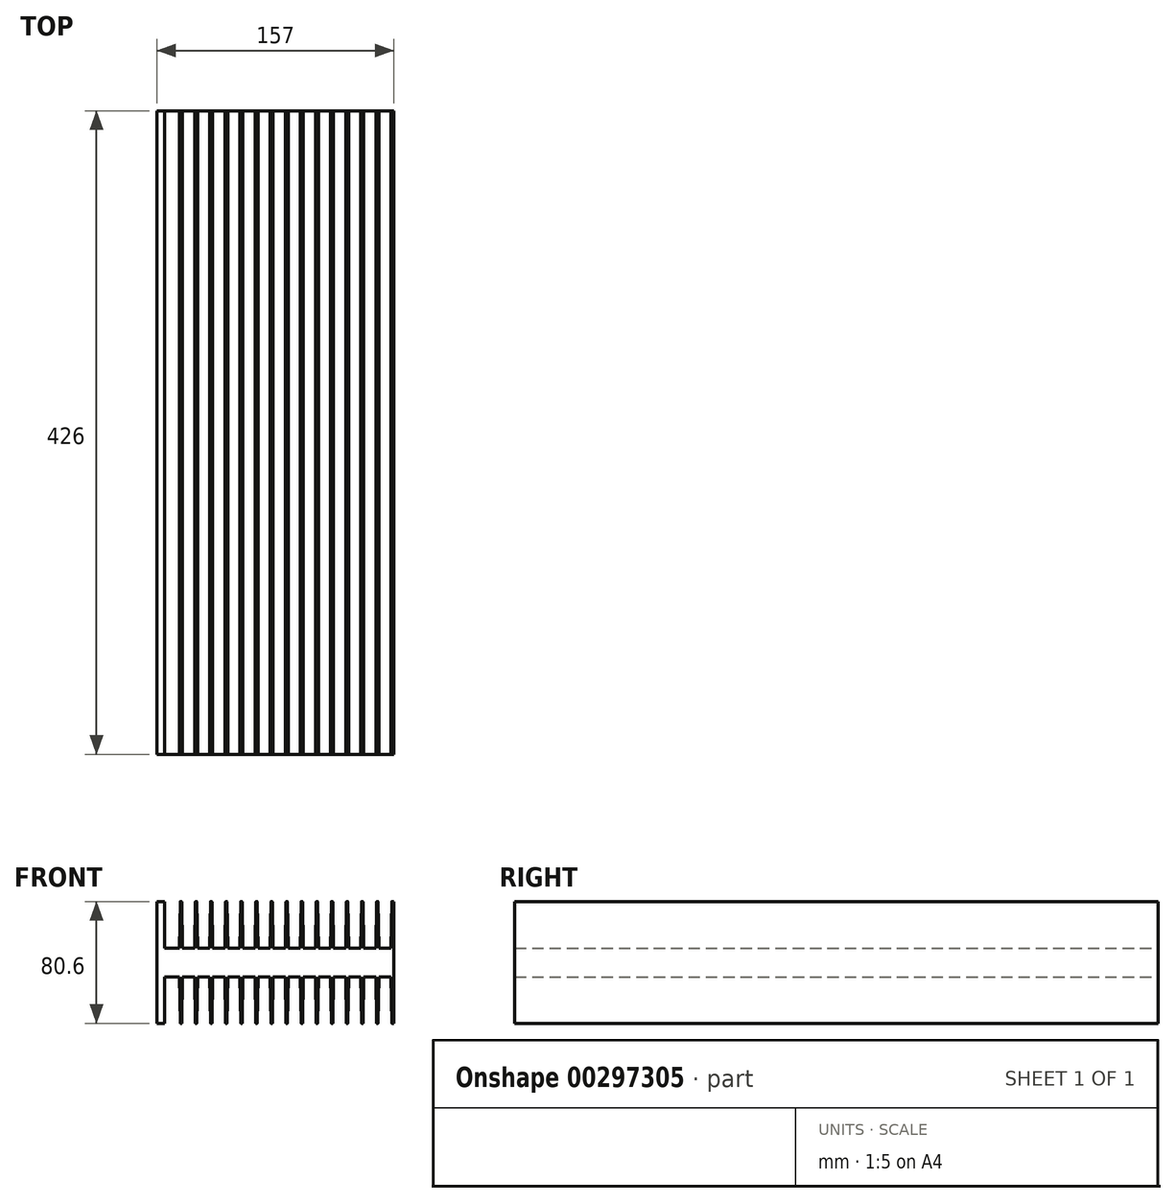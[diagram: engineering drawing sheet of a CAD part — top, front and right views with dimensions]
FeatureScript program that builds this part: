
annotation { "Feature Type Name" : "Feature", "Feature Type Description" : "" }
export const myFeature = defineFeature(function(context is Context, id is Id, definition is map)
    precondition{}
    {
        {
            var Q0;
            Q0=qCreatedBy(makeId("Front.planeOp"),FACE);
            var sketch = newSketch(context, id + "F0", { "sketchPlane" : qUnion([Q0])});
            skLineSegment(sketch, "E0", {"start": v(0, 0) * mm, "end": v(-0.5, 30.68) * mm});
            skLineSegment(sketch, "E1", {"start": v(8, 0) * mm, "end": v(8.5, 30.68) * mm});
            skLineSegment(sketch, "E2", {"start": v(-0.62, 30.8) * mm, "end": v(-1.5, 30.8) * mm});
            skLineSegment(sketch, "E3", {"start": v(-1.5, 30.8) * mm, "end": v(-2, 30.8) * mm});
            skLineSegment(sketch, "E4", {"start": v(-2, 30.8) * mm, "end": v(-2, -9.5) * mm});
            skLineSegment(sketch, "E5", {"start": v(-2, -9.5) * mm, "end": v(155, -9.5) * mm});
            skLineSegment(sketch, "E6", {"start": v(150, 30.8) * mm, "end": v(155, 30.8) * mm});
            skLineSegment(sketch, "E7", {"start": v(155, 30.8) * mm, "end": v(155, -9.5) * mm});
            skLineSegment(sketch, "E8", {"start": v(8, 0) * mm, "end": v(10, 0) * mm, "construction": true});
            skLineSegment(sketch, "E9", {"start": v(9, 0) * mm, "end": v(9, 30.8) * mm});
            skLineSegment(sketch, "E10", {"start": v(9, 30.8) * mm, "end": v(9, 0) * mm, "construction": true});
            skPoint(sketch, "E11.visualSharp", {"position": v(8.5, 30.8) * mm});
            skArc(sketch, "E11.filletArc", {"start": v(8.62, 30.8) * mm, "mid": v(8.53, 30.76) * mm, "end": v(8.5, 30.68) * mm});
            skPoint(sketch, "E12.visualSharp", {"position": v(9.5, 30.8) * mm});
            skPoint(sketch, "E13.visualSharp", {"position": v(-0.5, 30.8) * mm});
            skArc(sketch, "E13.filletArc", {"start": v(-0.5, 30.68) * mm, "mid": v(-0.53, 30.76) * mm, "end": v(-0.62, 30.8) * mm});
            skLineSegment(sketch, "E14", {"start": v(0, 0) * mm, "end": v(8, 0) * mm});
            skLineSegment(sketch, "E15", {"start": v(10, 0) * mm, "end": v(9.5, 30.68) * mm});
            skLineSegment(sketch, "E16", {"start": v(8.62, 30.8) * mm, "end": v(9.38, 30.8) * mm});
            skArc(sketch, "E17.filletArc", {"start": v(9.5, 30.68) * mm, "mid": v(9.47, 30.76) * mm, "end": v(9.38, 30.8) * mm});
            skLineSegment(sketch, "E18.1.0.0", {"start": v(10, 0) * mm, "end": v(18, 0) * mm});
            skLineSegment(sketch, "E18.1.0.1", {"start": v(18, 0) * mm, "end": v(18.5, 30.68) * mm});
            skArc(sketch, "E18.1.0.2", {"start": v(18.62, 30.8) * mm, "mid": v(18.53, 30.76) * mm, "end": v(18.5, 30.68) * mm});
            skLineSegment(sketch, "E18.1.0.3", {"start": v(18.62, 30.8) * mm, "end": v(19.38, 30.8) * mm});
            skArc(sketch, "E18.1.0.4", {"start": v(19.5, 30.68) * mm, "mid": v(19.47, 30.76) * mm, "end": v(19.38, 30.8) * mm});
            skLineSegment(sketch, "E18.1.0.5", {"start": v(20, 0) * mm, "end": v(19.5, 30.68) * mm});
            skLineSegment(sketch, "E18.2.0.0", {"start": v(20, 0) * mm, "end": v(28, 0) * mm});
            skLineSegment(sketch, "E18.2.0.1", {"start": v(28, 0) * mm, "end": v(28.5, 30.68) * mm});
            skArc(sketch, "E18.2.0.2", {"start": v(28.62, 30.8) * mm, "mid": v(28.53, 30.76) * mm, "end": v(28.5, 30.68) * mm});
            skLineSegment(sketch, "E18.2.0.3", {"start": v(28.62, 30.8) * mm, "end": v(29.38, 30.8) * mm});
            skArc(sketch, "E18.2.0.4", {"start": v(29.5, 30.68) * mm, "mid": v(29.47, 30.76) * mm, "end": v(29.38, 30.8) * mm});
            skLineSegment(sketch, "E18.2.0.5", {"start": v(30, 0) * mm, "end": v(29.5, 30.68) * mm});
            skLineSegment(sketch, "E18.3.0.0", {"start": v(30, 0) * mm, "end": v(38, 0) * mm});
            skLineSegment(sketch, "E18.3.0.1", {"start": v(38, 0) * mm, "end": v(38.5, 30.68) * mm});
            skArc(sketch, "E18.3.0.2", {"start": v(38.62, 30.8) * mm, "mid": v(38.53, 30.76) * mm, "end": v(38.5, 30.68) * mm});
            skLineSegment(sketch, "E18.3.0.3", {"start": v(38.62, 30.8) * mm, "end": v(39.38, 30.8) * mm});
            skArc(sketch, "E18.3.0.4", {"start": v(39.5, 30.68) * mm, "mid": v(39.47, 30.76) * mm, "end": v(39.38, 30.8) * mm});
            skLineSegment(sketch, "E18.3.0.5", {"start": v(40, 0) * mm, "end": v(39.5, 30.68) * mm});
            skLineSegment(sketch, "E18.4.0.0", {"start": v(40, 0) * mm, "end": v(48, 0) * mm});
            skLineSegment(sketch, "E18.4.0.1", {"start": v(48, 0) * mm, "end": v(48.5, 30.68) * mm});
            skArc(sketch, "E18.4.0.2", {"start": v(48.62, 30.8) * mm, "mid": v(48.53, 30.76) * mm, "end": v(48.5, 30.68) * mm});
            skLineSegment(sketch, "E18.4.0.3", {"start": v(48.62, 30.8) * mm, "end": v(49.38, 30.8) * mm});
            skArc(sketch, "E18.4.0.4", {"start": v(49.5, 30.68) * mm, "mid": v(49.47, 30.76) * mm, "end": v(49.38, 30.8) * mm});
            skLineSegment(sketch, "E18.4.0.5", {"start": v(50, 0) * mm, "end": v(49.5, 30.68) * mm});
            skLineSegment(sketch, "E18.5.0.0", {"start": v(50, 0) * mm, "end": v(58, 0) * mm});
            skLineSegment(sketch, "E18.5.0.1", {"start": v(58, 0) * mm, "end": v(58.5, 30.68) * mm});
            skArc(sketch, "E18.5.0.2", {"start": v(58.62, 30.8) * mm, "mid": v(58.53, 30.76) * mm, "end": v(58.5, 30.68) * mm});
            skLineSegment(sketch, "E18.5.0.3", {"start": v(58.62, 30.8) * mm, "end": v(59.38, 30.8) * mm});
            skArc(sketch, "E18.5.0.4", {"start": v(59.5, 30.68) * mm, "mid": v(59.47, 30.76) * mm, "end": v(59.38, 30.8) * mm});
            skLineSegment(sketch, "E18.5.0.5", {"start": v(60, 0) * mm, "end": v(59.5, 30.68) * mm});
            skLineSegment(sketch, "E18.6.0.0", {"start": v(60, 0) * mm, "end": v(68, 0) * mm});
            skLineSegment(sketch, "E18.6.0.1", {"start": v(68, 0) * mm, "end": v(68.5, 30.68) * mm});
            skArc(sketch, "E18.6.0.2", {"start": v(68.62, 30.8) * mm, "mid": v(68.53, 30.76) * mm, "end": v(68.5, 30.68) * mm});
            skLineSegment(sketch, "E18.6.0.3", {"start": v(68.62, 30.8) * mm, "end": v(69.38, 30.8) * mm});
            skArc(sketch, "E18.6.0.4", {"start": v(69.5, 30.68) * mm, "mid": v(69.47, 30.76) * mm, "end": v(69.38, 30.8) * mm});
            skLineSegment(sketch, "E18.6.0.5", {"start": v(70, 0) * mm, "end": v(69.5, 30.68) * mm});
            skLineSegment(sketch, "E18.7.0.0", {"start": v(70, 0) * mm, "end": v(78, 0) * mm});
            skLineSegment(sketch, "E18.7.0.1", {"start": v(78, 0) * mm, "end": v(78.5, 30.68) * mm});
            skArc(sketch, "E18.7.0.2", {"start": v(78.62, 30.8) * mm, "mid": v(78.53, 30.76) * mm, "end": v(78.5, 30.68) * mm});
            skLineSegment(sketch, "E18.7.0.3", {"start": v(78.62, 30.8) * mm, "end": v(79.38, 30.8) * mm});
            skArc(sketch, "E18.7.0.4", {"start": v(79.5, 30.68) * mm, "mid": v(79.47, 30.76) * mm, "end": v(79.38, 30.8) * mm});
            skLineSegment(sketch, "E18.7.0.5", {"start": v(80, 0) * mm, "end": v(79.5, 30.68) * mm});
            skLineSegment(sketch, "E18.8.0.0", {"start": v(80, 0) * mm, "end": v(88, 0) * mm});
            skLineSegment(sketch, "E18.8.0.1", {"start": v(88, 0) * mm, "end": v(88.5, 30.68) * mm});
            skArc(sketch, "E18.8.0.2", {"start": v(88.62, 30.8) * mm, "mid": v(88.53, 30.76) * mm, "end": v(88.5, 30.68) * mm});
            skLineSegment(sketch, "E18.8.0.3", {"start": v(88.62, 30.8) * mm, "end": v(89.38, 30.8) * mm});
            skArc(sketch, "E18.8.0.4", {"start": v(89.5, 30.68) * mm, "mid": v(89.47, 30.76) * mm, "end": v(89.38, 30.8) * mm});
            skLineSegment(sketch, "E18.8.0.5", {"start": v(90, 0) * mm, "end": v(89.5, 30.68) * mm});
            skLineSegment(sketch, "E18.9.0.0", {"start": v(90, 0) * mm, "end": v(98, 0) * mm});
            skLineSegment(sketch, "E18.9.0.1", {"start": v(98, 0) * mm, "end": v(98.5, 30.68) * mm});
            skArc(sketch, "E18.9.0.2", {"start": v(98.62, 30.8) * mm, "mid": v(98.53, 30.76) * mm, "end": v(98.5, 30.68) * mm});
            skLineSegment(sketch, "E18.9.0.3", {"start": v(98.62, 30.8) * mm, "end": v(99.38, 30.8) * mm});
            skArc(sketch, "E18.9.0.4", {"start": v(99.5, 30.68) * mm, "mid": v(99.47, 30.76) * mm, "end": v(99.38, 30.8) * mm});
            skLineSegment(sketch, "E18.9.0.5", {"start": v(100, 0) * mm, "end": v(99.5, 30.68) * mm});
            skLineSegment(sketch, "E18.10.0.0", {"start": v(100, 0) * mm, "end": v(108, 0) * mm});
            skLineSegment(sketch, "E18.10.0.1", {"start": v(108, 0) * mm, "end": v(108.5, 30.68) * mm});
            skArc(sketch, "E18.10.0.2", {"start": v(108.62, 30.8) * mm, "mid": v(108.53, 30.76) * mm, "end": v(108.5, 30.68) * mm});
            skLineSegment(sketch, "E18.10.0.3", {"start": v(108.62, 30.8) * mm, "end": v(109.38, 30.8) * mm});
            skArc(sketch, "E18.10.0.4", {"start": v(109.5, 30.68) * mm, "mid": v(109.47, 30.76) * mm, "end": v(109.38, 30.8) * mm});
            skLineSegment(sketch, "E18.10.0.5", {"start": v(110, 0) * mm, "end": v(109.5, 30.68) * mm});
            skLineSegment(sketch, "E18.11.0.0", {"start": v(110, 0) * mm, "end": v(118, 0) * mm});
            skLineSegment(sketch, "E18.11.0.1", {"start": v(118, 0) * mm, "end": v(118.5, 30.68) * mm});
            skArc(sketch, "E18.11.0.2", {"start": v(118.62, 30.8) * mm, "mid": v(118.53, 30.76) * mm, "end": v(118.5, 30.68) * mm});
            skLineSegment(sketch, "E18.11.0.3", {"start": v(118.62, 30.8) * mm, "end": v(119.38, 30.8) * mm});
            skArc(sketch, "E18.11.0.4", {"start": v(119.5, 30.68) * mm, "mid": v(119.47, 30.76) * mm, "end": v(119.38, 30.8) * mm});
            skLineSegment(sketch, "E18.11.0.5", {"start": v(120, 0) * mm, "end": v(119.5, 30.68) * mm});
            skLineSegment(sketch, "E18.12.0.0", {"start": v(120, 0) * mm, "end": v(128, 0) * mm});
            skLineSegment(sketch, "E18.12.0.1", {"start": v(128, 0) * mm, "end": v(128.5, 30.68) * mm});
            skArc(sketch, "E18.12.0.2", {"start": v(128.62, 30.8) * mm, "mid": v(128.53, 30.76) * mm, "end": v(128.5, 30.68) * mm});
            skLineSegment(sketch, "E18.12.0.3", {"start": v(128.62, 30.8) * mm, "end": v(129.38, 30.8) * mm});
            skArc(sketch, "E18.12.0.4", {"start": v(129.5, 30.68) * mm, "mid": v(129.47, 30.76) * mm, "end": v(129.38, 30.8) * mm});
            skLineSegment(sketch, "E18.12.0.5", {"start": v(130, 0) * mm, "end": v(129.5, 30.68) * mm});
            skLineSegment(sketch, "E18.13.0.0", {"start": v(130, 0) * mm, "end": v(138, 0) * mm});
            skLineSegment(sketch, "E18.13.0.1", {"start": v(138, 0) * mm, "end": v(138.5, 30.68) * mm});
            skArc(sketch, "E18.13.0.2", {"start": v(138.62, 30.8) * mm, "mid": v(138.53, 30.76) * mm, "end": v(138.5, 30.68) * mm});
            skLineSegment(sketch, "E18.13.0.3", {"start": v(138.62, 30.8) * mm, "end": v(139.38, 30.8) * mm});
            skArc(sketch, "E18.13.0.4", {"start": v(139.5, 30.68) * mm, "mid": v(139.47, 30.76) * mm, "end": v(139.38, 30.8) * mm});
            skLineSegment(sketch, "E18.13.0.5", {"start": v(140, 0) * mm, "end": v(139.5, 30.68) * mm});
            skLineSegment(sketch, "E18.direction1", {"start": v(0, 0) * mm, "end": v(10, 0) * mm, "construction": true});
            skLineSegment(sketch, "E19", {"start": v(140, 0) * mm, "end": v(150, 0) * mm});
            skLineSegment(sketch, "E20", {"start": v(150, 30.8) * mm, "end": v(150, 0) * mm});
            skSolve(sketch);
        }
        {
            var Q0;
            Q0=qSketchRegion(id+"F0",true);
            extrude(context, id + "F1", {"entities" : qUnion([Q0]), "depth" : 426 * mm});
        }
        {
            var Q0;
            Q0=makeQuery(id+"F1.opExtrude","SWEPT_BODY",BODY,{"disambiguationData":[OSD([sQuery(id+"F0.wireOp",EDGE,"E0"),sQuery(id+"F0.wireOp",EDGE,"E1"),sQuery(id+"F0.wireOp",EDGE,"E2"),sQuery(id+"F0.wireOp",EDGE,"E3"),sQuery(id+"F0.wireOp",EDGE,"E4"),sQuery(id+"F0.wireOp",EDGE,"E5"),sQuery(id+"F0.wireOp",EDGE,"E6"),sQuery(id+"F0.wireOp",EDGE,"E7"),sQuery(id+"F0.wireOp",EDGE,"E11.filletArc"),sQuery(id+"F0.wireOp",EDGE,"E13.filletArc"),sQuery(id+"F0.wireOp",EDGE,"E14"),sQuery(id+"F0.wireOp",EDGE,"E15"),sQuery(id+"F0.wireOp",EDGE,"E16"),sQuery(id+"F0.wireOp",EDGE,"E17.filletArc"),sQuery(id+"F0.wireOp",EDGE,"E18.1.0.0"),sQuery(id+"F0.wireOp",EDGE,"E18.1.0.1"),sQuery(id+"F0.wireOp",EDGE,"E18.1.0.2"),sQuery(id+"F0.wireOp",EDGE,"E18.1.0.3"),sQuery(id+"F0.wireOp",EDGE,"E18.1.0.4"),sQuery(id+"F0.wireOp",EDGE,"E18.1.0.5"),sQuery(id+"F0.wireOp",EDGE,"E18.2.0.0"),sQuery(id+"F0.wireOp",EDGE,"E18.2.0.1"),sQuery(id+"F0.wireOp",EDGE,"E18.2.0.2"),sQuery(id+"F0.wireOp",EDGE,"E18.2.0.3"),sQuery(id+"F0.wireOp",EDGE,"E18.2.0.4"),sQuery(id+"F0.wireOp",EDGE,"E18.2.0.5"),sQuery(id+"F0.wireOp",EDGE,"E18.3.0.0"),sQuery(id+"F0.wireOp",EDGE,"E18.3.0.1"),sQuery(id+"F0.wireOp",EDGE,"E18.3.0.2"),sQuery(id+"F0.wireOp",EDGE,"E18.3.0.3"),sQuery(id+"F0.wireOp",EDGE,"E18.3.0.4"),sQuery(id+"F0.wireOp",EDGE,"E18.3.0.5"),sQuery(id+"F0.wireOp",EDGE,"E18.4.0.0"),sQuery(id+"F0.wireOp",EDGE,"E18.4.0.1"),sQuery(id+"F0.wireOp",EDGE,"E18.4.0.2"),sQuery(id+"F0.wireOp",EDGE,"E18.4.0.3"),sQuery(id+"F0.wireOp",EDGE,"E18.4.0.4"),sQuery(id+"F0.wireOp",EDGE,"E18.4.0.5"),sQuery(id+"F0.wireOp",EDGE,"E18.5.0.0"),sQuery(id+"F0.wireOp",EDGE,"E18.5.0.1"),sQuery(id+"F0.wireOp",EDGE,"E18.5.0.2"),sQuery(id+"F0.wireOp",EDGE,"E18.5.0.3"),sQuery(id+"F0.wireOp",EDGE,"E18.5.0.4"),sQuery(id+"F0.wireOp",EDGE,"E18.5.0.5"),sQuery(id+"F0.wireOp",EDGE,"E18.6.0.0"),sQuery(id+"F0.wireOp",EDGE,"E18.6.0.1"),sQuery(id+"F0.wireOp",EDGE,"E18.6.0.2"),sQuery(id+"F0.wireOp",EDGE,"E18.6.0.3"),sQuery(id+"F0.wireOp",EDGE,"E18.6.0.4"),sQuery(id+"F0.wireOp",EDGE,"E18.6.0.5"),sQuery(id+"F0.wireOp",EDGE,"E18.7.0.0"),sQuery(id+"F0.wireOp",EDGE,"E18.7.0.1"),sQuery(id+"F0.wireOp",EDGE,"E18.7.0.2"),sQuery(id+"F0.wireOp",EDGE,"E18.7.0.3"),sQuery(id+"F0.wireOp",EDGE,"E18.7.0.4"),sQuery(id+"F0.wireOp",EDGE,"E18.7.0.5"),sQuery(id+"F0.wireOp",EDGE,"E18.8.0.0"),sQuery(id+"F0.wireOp",EDGE,"E18.8.0.1"),sQuery(id+"F0.wireOp",EDGE,"E18.8.0.2"),sQuery(id+"F0.wireOp",EDGE,"E18.8.0.3"),sQuery(id+"F0.wireOp",EDGE,"E18.8.0.4"),sQuery(id+"F0.wireOp",EDGE,"E18.8.0.5"),sQuery(id+"F0.wireOp",EDGE,"E18.9.0.0"),sQuery(id+"F0.wireOp",EDGE,"E18.9.0.1"),sQuery(id+"F0.wireOp",EDGE,"E18.9.0.2"),sQuery(id+"F0.wireOp",EDGE,"E18.9.0.3"),sQuery(id+"F0.wireOp",EDGE,"E18.9.0.4"),sQuery(id+"F0.wireOp",EDGE,"E18.9.0.5"),sQuery(id+"F0.wireOp",EDGE,"E18.10.0.0"),sQuery(id+"F0.wireOp",EDGE,"E18.10.0.1"),sQuery(id+"F0.wireOp",EDGE,"E18.10.0.2"),sQuery(id+"F0.wireOp",EDGE,"E18.10.0.3"),sQuery(id+"F0.wireOp",EDGE,"E18.10.0.4"),sQuery(id+"F0.wireOp",EDGE,"E18.10.0.5"),sQuery(id+"F0.wireOp",EDGE,"E18.11.0.0"),sQuery(id+"F0.wireOp",EDGE,"E18.11.0.1"),sQuery(id+"F0.wireOp",EDGE,"E18.11.0.2"),sQuery(id+"F0.wireOp",EDGE,"E18.11.0.3"),sQuery(id+"F0.wireOp",EDGE,"E18.11.0.4"),sQuery(id+"F0.wireOp",EDGE,"E18.11.0.5"),sQuery(id+"F0.wireOp",EDGE,"E18.12.0.0"),sQuery(id+"F0.wireOp",EDGE,"E18.12.0.1"),sQuery(id+"F0.wireOp",EDGE,"E18.12.0.2"),sQuery(id+"F0.wireOp",EDGE,"E18.12.0.3"),sQuery(id+"F0.wireOp",EDGE,"E18.12.0.4"),sQuery(id+"F0.wireOp",EDGE,"E18.12.0.5"),sQuery(id+"F0.wireOp",EDGE,"E18.13.0.0"),sQuery(id+"F0.wireOp",EDGE,"E18.13.0.1"),sQuery(id+"F0.wireOp",EDGE,"E18.13.0.2"),sQuery(id+"F0.wireOp",EDGE,"E18.13.0.3"),sQuery(id+"F0.wireOp",EDGE,"E18.13.0.4"),sQuery(id+"F0.wireOp",EDGE,"E18.13.0.5"),sQuery(id+"F0.wireOp",EDGE,"E19"),sQuery(id+"F0.wireOp",EDGE,"E20")])]});
            var Q1;
            Q1=makeQuery(id+"F1.opExtrude","SWEPT_EDGE",EDGE,{"disambiguationData":[OSD([sQuery(id+"F0.wireOp",EDGE,"E5"),sQuery(id+"F0.wireOp",EDGE,"E7")])]});
            transform(context, id + "F2", {"entities" : qUnion([Q0]), "transformType" : TransformType.ROTATION, "transformAxis" : qUnion([Q1]), "angle" : 180 * degree, "makeCopy" : false});
        }
        {
            var Q0;
            Q0=makeQuery(id+"F1.opExtrude","SWEPT_BODY",BODY,{"disambiguationData":[OSD([sQuery(id+"F0.wireOp",EDGE,"E0"),sQuery(id+"F0.wireOp",EDGE,"E1"),sQuery(id+"F0.wireOp",EDGE,"E2"),sQuery(id+"F0.wireOp",EDGE,"E3"),sQuery(id+"F0.wireOp",EDGE,"E4"),sQuery(id+"F0.wireOp",EDGE,"E5"),sQuery(id+"F0.wireOp",EDGE,"E6"),sQuery(id+"F0.wireOp",EDGE,"E7"),sQuery(id+"F0.wireOp",EDGE,"E11.filletArc"),sQuery(id+"F0.wireOp",EDGE,"E13.filletArc"),sQuery(id+"F0.wireOp",EDGE,"E14"),sQuery(id+"F0.wireOp",EDGE,"E15"),sQuery(id+"F0.wireOp",EDGE,"E16"),sQuery(id+"F0.wireOp",EDGE,"E17.filletArc"),sQuery(id+"F0.wireOp",EDGE,"E18.1.0.0"),sQuery(id+"F0.wireOp",EDGE,"E18.1.0.1"),sQuery(id+"F0.wireOp",EDGE,"E18.1.0.2"),sQuery(id+"F0.wireOp",EDGE,"E18.1.0.3"),sQuery(id+"F0.wireOp",EDGE,"E18.1.0.4"),sQuery(id+"F0.wireOp",EDGE,"E18.1.0.5"),sQuery(id+"F0.wireOp",EDGE,"E18.2.0.0"),sQuery(id+"F0.wireOp",EDGE,"E18.2.0.1"),sQuery(id+"F0.wireOp",EDGE,"E18.2.0.2"),sQuery(id+"F0.wireOp",EDGE,"E18.2.0.3"),sQuery(id+"F0.wireOp",EDGE,"E18.2.0.4"),sQuery(id+"F0.wireOp",EDGE,"E18.2.0.5"),sQuery(id+"F0.wireOp",EDGE,"E18.3.0.0"),sQuery(id+"F0.wireOp",EDGE,"E18.3.0.1"),sQuery(id+"F0.wireOp",EDGE,"E18.3.0.2"),sQuery(id+"F0.wireOp",EDGE,"E18.3.0.3"),sQuery(id+"F0.wireOp",EDGE,"E18.3.0.4"),sQuery(id+"F0.wireOp",EDGE,"E18.3.0.5"),sQuery(id+"F0.wireOp",EDGE,"E18.4.0.0"),sQuery(id+"F0.wireOp",EDGE,"E18.4.0.1"),sQuery(id+"F0.wireOp",EDGE,"E18.4.0.2"),sQuery(id+"F0.wireOp",EDGE,"E18.4.0.3"),sQuery(id+"F0.wireOp",EDGE,"E18.4.0.4"),sQuery(id+"F0.wireOp",EDGE,"E18.4.0.5"),sQuery(id+"F0.wireOp",EDGE,"E18.5.0.0"),sQuery(id+"F0.wireOp",EDGE,"E18.5.0.1"),sQuery(id+"F0.wireOp",EDGE,"E18.5.0.2"),sQuery(id+"F0.wireOp",EDGE,"E18.5.0.3"),sQuery(id+"F0.wireOp",EDGE,"E18.5.0.4"),sQuery(id+"F0.wireOp",EDGE,"E18.5.0.5"),sQuery(id+"F0.wireOp",EDGE,"E18.6.0.0"),sQuery(id+"F0.wireOp",EDGE,"E18.6.0.1"),sQuery(id+"F0.wireOp",EDGE,"E18.6.0.2"),sQuery(id+"F0.wireOp",EDGE,"E18.6.0.3"),sQuery(id+"F0.wireOp",EDGE,"E18.6.0.4"),sQuery(id+"F0.wireOp",EDGE,"E18.6.0.5"),sQuery(id+"F0.wireOp",EDGE,"E18.7.0.0"),sQuery(id+"F0.wireOp",EDGE,"E18.7.0.1"),sQuery(id+"F0.wireOp",EDGE,"E18.7.0.2"),sQuery(id+"F0.wireOp",EDGE,"E18.7.0.3"),sQuery(id+"F0.wireOp",EDGE,"E18.7.0.4"),sQuery(id+"F0.wireOp",EDGE,"E18.7.0.5"),sQuery(id+"F0.wireOp",EDGE,"E18.8.0.0"),sQuery(id+"F0.wireOp",EDGE,"E18.8.0.1"),sQuery(id+"F0.wireOp",EDGE,"E18.8.0.2"),sQuery(id+"F0.wireOp",EDGE,"E18.8.0.3"),sQuery(id+"F0.wireOp",EDGE,"E18.8.0.4"),sQuery(id+"F0.wireOp",EDGE,"E18.8.0.5"),sQuery(id+"F0.wireOp",EDGE,"E18.9.0.0"),sQuery(id+"F0.wireOp",EDGE,"E18.9.0.1"),sQuery(id+"F0.wireOp",EDGE,"E18.9.0.2"),sQuery(id+"F0.wireOp",EDGE,"E18.9.0.3"),sQuery(id+"F0.wireOp",EDGE,"E18.9.0.4"),sQuery(id+"F0.wireOp",EDGE,"E18.9.0.5"),sQuery(id+"F0.wireOp",EDGE,"E18.10.0.0"),sQuery(id+"F0.wireOp",EDGE,"E18.10.0.1"),sQuery(id+"F0.wireOp",EDGE,"E18.10.0.2"),sQuery(id+"F0.wireOp",EDGE,"E18.10.0.3"),sQuery(id+"F0.wireOp",EDGE,"E18.10.0.4"),sQuery(id+"F0.wireOp",EDGE,"E18.10.0.5"),sQuery(id+"F0.wireOp",EDGE,"E18.11.0.0"),sQuery(id+"F0.wireOp",EDGE,"E18.11.0.1"),sQuery(id+"F0.wireOp",EDGE,"E18.11.0.2"),sQuery(id+"F0.wireOp",EDGE,"E18.11.0.3"),sQuery(id+"F0.wireOp",EDGE,"E18.11.0.4"),sQuery(id+"F0.wireOp",EDGE,"E18.11.0.5"),sQuery(id+"F0.wireOp",EDGE,"E18.12.0.0"),sQuery(id+"F0.wireOp",EDGE,"E18.12.0.1"),sQuery(id+"F0.wireOp",EDGE,"E18.12.0.2"),sQuery(id+"F0.wireOp",EDGE,"E18.12.0.3"),sQuery(id+"F0.wireOp",EDGE,"E18.12.0.4"),sQuery(id+"F0.wireOp",EDGE,"E18.12.0.5"),sQuery(id+"F0.wireOp",EDGE,"E18.13.0.0"),sQuery(id+"F0.wireOp",EDGE,"E18.13.0.1"),sQuery(id+"F0.wireOp",EDGE,"E18.13.0.2"),sQuery(id+"F0.wireOp",EDGE,"E18.13.0.3"),sQuery(id+"F0.wireOp",EDGE,"E18.13.0.4"),sQuery(id+"F0.wireOp",EDGE,"E18.13.0.5"),sQuery(id+"F0.wireOp",EDGE,"E19"),sQuery(id+"F0.wireOp",EDGE,"E20")])]});
            transform(context, id + "F3", {"entities" : qUnion([Q0]), "transformType" : TransformType.TRANSLATION_3D, "dx" : -179 * mm, "dy" : -94 * mm, "dz" : 509.5 * mm, "makeCopy" : false});
        }
        {
            var Q0;
            Q0=makeQuery(id+"F1.opExtrude","SWEPT_BODY",BODY,{"disambiguationData":[OSD([sQuery(id+"F0.wireOp",EDGE,"E0"),sQuery(id+"F0.wireOp",EDGE,"E1"),sQuery(id+"F0.wireOp",EDGE,"E2"),sQuery(id+"F0.wireOp",EDGE,"E3"),sQuery(id+"F0.wireOp",EDGE,"E4"),sQuery(id+"F0.wireOp",EDGE,"E5"),sQuery(id+"F0.wireOp",EDGE,"E6"),sQuery(id+"F0.wireOp",EDGE,"E7"),sQuery(id+"F0.wireOp",EDGE,"E11.filletArc"),sQuery(id+"F0.wireOp",EDGE,"E13.filletArc"),sQuery(id+"F0.wireOp",EDGE,"E14"),sQuery(id+"F0.wireOp",EDGE,"E15"),sQuery(id+"F0.wireOp",EDGE,"E16"),sQuery(id+"F0.wireOp",EDGE,"E17.filletArc"),sQuery(id+"F0.wireOp",EDGE,"E18.1.0.0"),sQuery(id+"F0.wireOp",EDGE,"E18.1.0.1"),sQuery(id+"F0.wireOp",EDGE,"E18.1.0.2"),sQuery(id+"F0.wireOp",EDGE,"E18.1.0.3"),sQuery(id+"F0.wireOp",EDGE,"E18.1.0.4"),sQuery(id+"F0.wireOp",EDGE,"E18.1.0.5"),sQuery(id+"F0.wireOp",EDGE,"E18.2.0.0"),sQuery(id+"F0.wireOp",EDGE,"E18.2.0.1"),sQuery(id+"F0.wireOp",EDGE,"E18.2.0.2"),sQuery(id+"F0.wireOp",EDGE,"E18.2.0.3"),sQuery(id+"F0.wireOp",EDGE,"E18.2.0.4"),sQuery(id+"F0.wireOp",EDGE,"E18.2.0.5"),sQuery(id+"F0.wireOp",EDGE,"E18.3.0.0"),sQuery(id+"F0.wireOp",EDGE,"E18.3.0.1"),sQuery(id+"F0.wireOp",EDGE,"E18.3.0.2"),sQuery(id+"F0.wireOp",EDGE,"E18.3.0.3"),sQuery(id+"F0.wireOp",EDGE,"E18.3.0.4"),sQuery(id+"F0.wireOp",EDGE,"E18.3.0.5"),sQuery(id+"F0.wireOp",EDGE,"E18.4.0.0"),sQuery(id+"F0.wireOp",EDGE,"E18.4.0.1"),sQuery(id+"F0.wireOp",EDGE,"E18.4.0.2"),sQuery(id+"F0.wireOp",EDGE,"E18.4.0.3"),sQuery(id+"F0.wireOp",EDGE,"E18.4.0.4"),sQuery(id+"F0.wireOp",EDGE,"E18.4.0.5"),sQuery(id+"F0.wireOp",EDGE,"E18.5.0.0"),sQuery(id+"F0.wireOp",EDGE,"E18.5.0.1"),sQuery(id+"F0.wireOp",EDGE,"E18.5.0.2"),sQuery(id+"F0.wireOp",EDGE,"E18.5.0.3"),sQuery(id+"F0.wireOp",EDGE,"E18.5.0.4"),sQuery(id+"F0.wireOp",EDGE,"E18.5.0.5"),sQuery(id+"F0.wireOp",EDGE,"E18.6.0.0"),sQuery(id+"F0.wireOp",EDGE,"E18.6.0.1"),sQuery(id+"F0.wireOp",EDGE,"E18.6.0.2"),sQuery(id+"F0.wireOp",EDGE,"E18.6.0.3"),sQuery(id+"F0.wireOp",EDGE,"E18.6.0.4"),sQuery(id+"F0.wireOp",EDGE,"E18.6.0.5"),sQuery(id+"F0.wireOp",EDGE,"E18.7.0.0"),sQuery(id+"F0.wireOp",EDGE,"E18.7.0.1"),sQuery(id+"F0.wireOp",EDGE,"E18.7.0.2"),sQuery(id+"F0.wireOp",EDGE,"E18.7.0.3"),sQuery(id+"F0.wireOp",EDGE,"E18.7.0.4"),sQuery(id+"F0.wireOp",EDGE,"E18.7.0.5"),sQuery(id+"F0.wireOp",EDGE,"E18.8.0.0"),sQuery(id+"F0.wireOp",EDGE,"E18.8.0.1"),sQuery(id+"F0.wireOp",EDGE,"E18.8.0.2"),sQuery(id+"F0.wireOp",EDGE,"E18.8.0.3"),sQuery(id+"F0.wireOp",EDGE,"E18.8.0.4"),sQuery(id+"F0.wireOp",EDGE,"E18.8.0.5"),sQuery(id+"F0.wireOp",EDGE,"E18.9.0.0"),sQuery(id+"F0.wireOp",EDGE,"E18.9.0.1"),sQuery(id+"F0.wireOp",EDGE,"E18.9.0.2"),sQuery(id+"F0.wireOp",EDGE,"E18.9.0.3"),sQuery(id+"F0.wireOp",EDGE,"E18.9.0.4"),sQuery(id+"F0.wireOp",EDGE,"E18.9.0.5"),sQuery(id+"F0.wireOp",EDGE,"E18.10.0.0"),sQuery(id+"F0.wireOp",EDGE,"E18.10.0.1"),sQuery(id+"F0.wireOp",EDGE,"E18.10.0.2"),sQuery(id+"F0.wireOp",EDGE,"E18.10.0.3"),sQuery(id+"F0.wireOp",EDGE,"E18.10.0.4"),sQuery(id+"F0.wireOp",EDGE,"E18.10.0.5"),sQuery(id+"F0.wireOp",EDGE,"E18.11.0.0"),sQuery(id+"F0.wireOp",EDGE,"E18.11.0.1"),sQuery(id+"F0.wireOp",EDGE,"E18.11.0.2"),sQuery(id+"F0.wireOp",EDGE,"E18.11.0.3"),sQuery(id+"F0.wireOp",EDGE,"E18.11.0.4"),sQuery(id+"F0.wireOp",EDGE,"E18.11.0.5"),sQuery(id+"F0.wireOp",EDGE,"E18.12.0.0"),sQuery(id+"F0.wireOp",EDGE,"E18.12.0.1"),sQuery(id+"F0.wireOp",EDGE,"E18.12.0.2"),sQuery(id+"F0.wireOp",EDGE,"E18.12.0.3"),sQuery(id+"F0.wireOp",EDGE,"E18.12.0.4"),sQuery(id+"F0.wireOp",EDGE,"E18.12.0.5"),sQuery(id+"F0.wireOp",EDGE,"E18.13.0.0"),sQuery(id+"F0.wireOp",EDGE,"E18.13.0.1"),sQuery(id+"F0.wireOp",EDGE,"E18.13.0.2"),sQuery(id+"F0.wireOp",EDGE,"E18.13.0.3"),sQuery(id+"F0.wireOp",EDGE,"E18.13.0.4"),sQuery(id+"F0.wireOp",EDGE,"E18.13.0.5"),sQuery(id+"F0.wireOp",EDGE,"E19"),sQuery(id+"F0.wireOp",EDGE,"E20")])]});
            var Q1;
            Q1=makeQuery(id+"F1.opExtrude","SWEPT_FACE",FACE,{"disambiguationData":[OSD([sQuery(id+"F0.wireOp",EDGE,"E5")])]});
            mirror(context, id + "F4", {"operationType" : NewBodyOperationType.ADD, "entities" : qUnion([Q0]), "mirrorPlane" : qUnion([Q1])});
        }
    });
